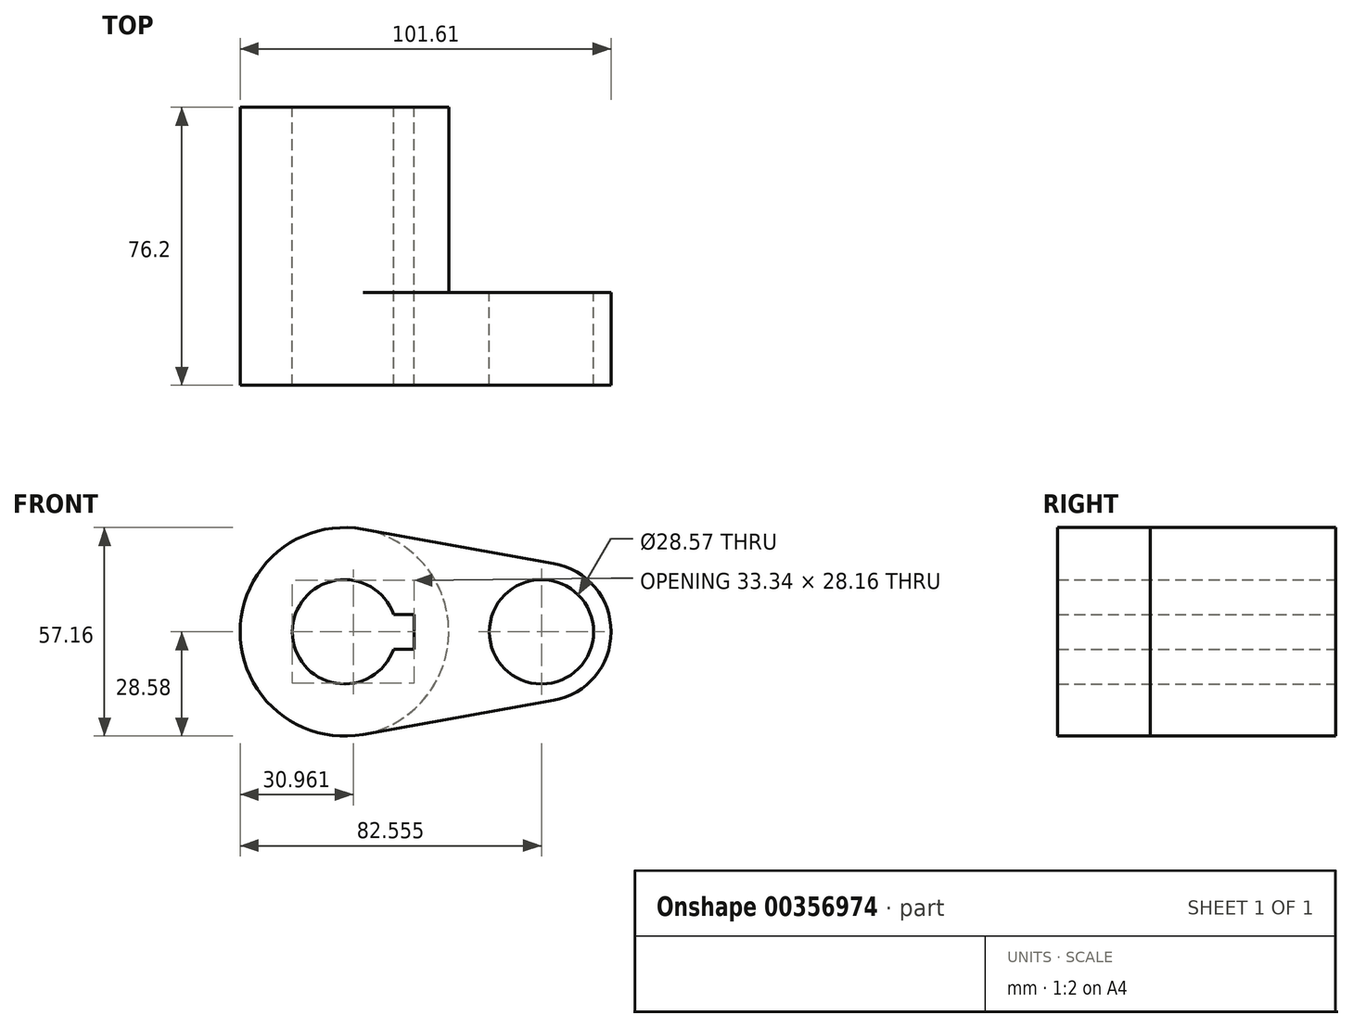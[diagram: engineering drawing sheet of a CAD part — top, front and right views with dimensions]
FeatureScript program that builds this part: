
annotation { "Feature Type Name" : "Feature", "Feature Type Description" : "" }
export const myFeature = defineFeature(function(context is Context, id is Id, definition is map)
    precondition{}
    {
        {
            var Q0;
            Q0=qCreatedBy(makeId("Front.planeOp"),FACE);
            var sketch = newSketch(context, id + "F0", { "sketchPlane" : qUnion([Q0])});
            skCircle(sketch, "E0", {"center": v(0, 0) * mm, "radius": 28.58 * mm});
            skCircle(sketch, "E1", {"center": v(53.97, 0) * mm, "radius": 19.05 * mm});
            skLineSegment(sketch, "E2", {"start": v(5.04, 28.13) * mm, "end": v(57.34, 18.75) * mm});
            skLineSegment(sketch, "E3", {"start": v(5.04, -28.13) * mm, "end": v(57.34, -18.75) * mm});
            skCircle(sketch, "E4", {"center": v(0, 0) * mm, "radius": 14.29 * mm});
            skCircle(sketch, "E5", {"center": v(53.97, 0) * mm, "radius": 14.29 * mm});
            skLineSegment(sketch, "E6.bottom", {"start": v(19.05, 4.76) * mm, "end": v(-19.05, 4.76) * mm});
            skLineSegment(sketch, "E6.top", {"start": v(19.05, -4.76) * mm, "end": v(-19.05, -4.76) * mm});
            skLineSegment(sketch, "E6.left", {"start": v(19.05, 4.76) * mm, "end": v(19.05, -4.76) * mm});
            skLineSegment(sketch, "E6.right", {"start": v(-19.05, 4.76) * mm, "end": v(-19.05, -4.76) * mm});
            skSolve(sketch);
        }
        {
            var Q0;
            {var subQ5=sQuery(id+"F0.wireOp",EDGE,"E6.right");Q0=makeQuery(id+"F0.imprint","IMPRINT",FACE,{"disambiguationData":[TD([[makeQuery(id+"F0.imprint","IMPRINT",EDGE,{"derivedFrom":subQ5}),1.0]])]});}
            var Q1;
            {var subQ7=sQuery(id+"F0.wireOp",EDGE,"E6.left");Q1=makeQuery(id+"F0.imprint","IMPRINT",FACE,{"disambiguationData":[TD([[makeQuery(id+"F0.imprint","IMPRINT",EDGE,{"derivedFrom":subQ7}),1.0]])]});}
            var Q2;
            Q2=makeQuery(id+"F0.imprint","IMPRINT",FACE,{"disambiguationData":[TD([[makeQuery(id+"F0.imprint","IMPRINT",EDGE,{"derivedFrom":sQuery(id+"F0.wireOp",EDGE,"E5")}),-1.0]])]});
            var Q3;
            {var subQ0=sQuery(id+"F0.wireOp",EDGE,"E2");Q3=makeQuery(id+"F0.imprint","IMPRINT",FACE,{"disambiguationData":[TD([[makeQuery(id+"F0.imprint","IMPRINT",EDGE,{"derivedFrom":subQ0}),-1.0]])]});}
            extrude(context, id + "F1", {"entities" : qUnion([Q0, Q1, Q2, Q3]), "depth" : 25.4 * mm});
        }
        {
            var Q0;
            {var subQ5=sQuery(id+"F0.wireOp",EDGE,"E6.right");Q0=makeQuery(id+"F0.imprint","IMPRINT",FACE,{"disambiguationData":[TD([[makeQuery(id+"F0.imprint","IMPRINT",EDGE,{"derivedFrom":subQ5}),1.0]])]});}
            var Q1;
            {var subQ7=sQuery(id+"F0.wireOp",EDGE,"E6.left");Q1=makeQuery(id+"F0.imprint","IMPRINT",FACE,{"disambiguationData":[TD([[makeQuery(id+"F0.imprint","IMPRINT",EDGE,{"derivedFrom":subQ7}),1.0]])]});}
            extrude(context, id + "F2", {"entities" : qUnion([Q0, Q1]), "operationType" : NewBodyOperationType.ADD, "oppositeDirection" : true, "depth" : 50.8 * mm});
        }
    });
